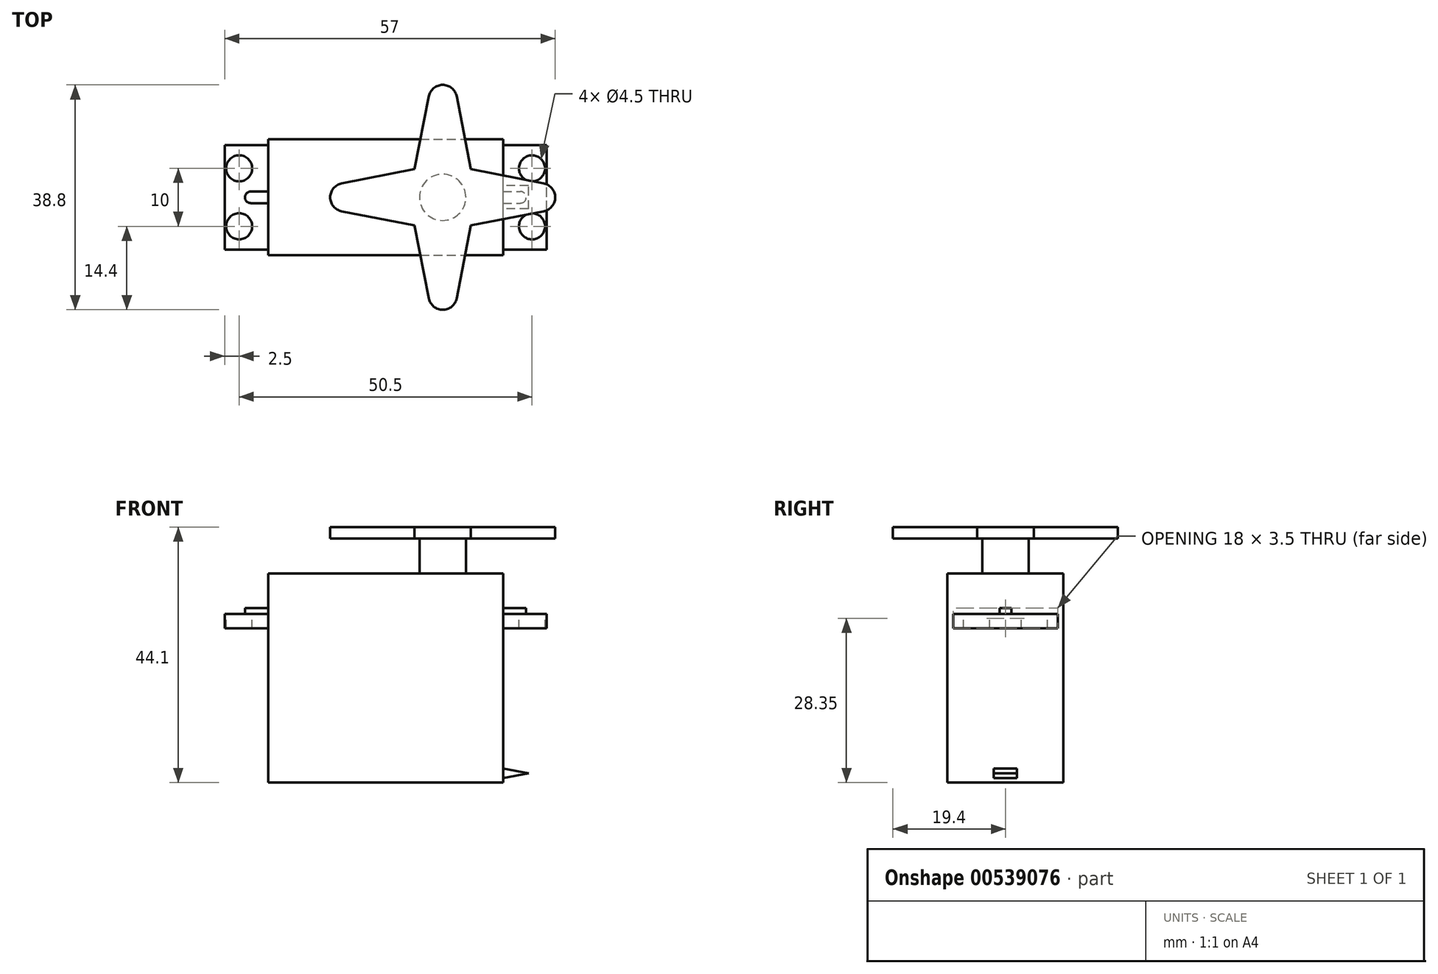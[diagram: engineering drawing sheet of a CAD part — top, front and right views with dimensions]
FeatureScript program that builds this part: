
annotation { "Feature Type Name" : "Feature", "Feature Type Description" : "" }
export const myFeature = defineFeature(function(context is Context, id is Id, definition is map)
    precondition{}
    {
        {
            var Q0;
            Q0=qCreatedBy(makeId("Front.planeOp"),FACE);
            var sketch = newSketch(context, id + "F0", { "sketchPlane" : qUnion([Q0])});
            skLineSegment(sketch, "E0.bottom", {"start": v(0, 0) * mm, "end": v(40.5, 0) * mm});
            skLineSegment(sketch, "E0.top", {"start": v(0, 36.1) * mm, "end": v(40.5, 36.1) * mm});
            skLineSegment(sketch, "E0.left", {"start": v(0, 0) * mm, "end": v(0, 36.1) * mm});
            skLineSegment(sketch, "E0.right", {"start": v(40.5, 0) * mm, "end": v(40.5, 36.1) * mm});
            skLineSegment(sketch, "E1.bottom", {"start": v(40.5, 26.6) * mm, "end": v(48, 26.6) * mm});
            skLineSegment(sketch, "E1.top", {"start": v(40.5, 29.1) * mm, "end": v(48, 29.1) * mm});
            skLineSegment(sketch, "E1.left", {"start": v(40.5, 26.6) * mm, "end": v(40.5, 29.1) * mm});
            skLineSegment(sketch, "E1.right", {"start": v(48, 26.6) * mm, "end": v(48, 29.1) * mm});
            skLineSegment(sketch, "E2.bottom", {"start": v(0, 26.6) * mm, "end": v(-7.5, 26.6) * mm});
            skLineSegment(sketch, "E2.top", {"start": v(0, 29.1) * mm, "end": v(-7.5, 29.1) * mm});
            skLineSegment(sketch, "E2.left", {"start": v(0, 26.6) * mm, "end": v(0, 29.1) * mm});
            skLineSegment(sketch, "E2.right", {"start": v(-7.5, 26.6) * mm, "end": v(-7.5, 29.1) * mm});
            skLineSegment(sketch, "E3", {"start": v(40.5, 2.42) * mm, "end": v(44.9, 1.62) * mm});
            skLineSegment(sketch, "E4", {"start": v(44.9, 1.62) * mm, "end": v(40.5, 0.82) * mm});
            skLineSegment(sketch, "E5", {"start": v(30.1, 44.1) * mm, "end": v(30.1, 36.1) * mm, "construction": true});
            skSolve(sketch);
        }
        {
            var Q0;
            {var subQ3=sQuery(id+"F0.wireOp",EDGE,"E0.bottom");Q0=makeQuery(id+"F0.imprint","IMPRINT",FACE,{"disambiguationData":[TD([[makeQuery(id+"F0.imprint","IMPRINT",EDGE,{"derivedFrom":subQ3}),1.0]])]});}
            extrude(context, id + "F1", {"entities" : qUnion([Q0]), "depth" : 20 * mm, "offsetDistance" : 25 * mm, "symmetric" : true});
        }
        {
            var Q0;
            Q0=makeQuery(id+"F0.imprint","IMPRINT",FACE,{"disambiguationData":[TD([[makeQuery(id+"F0.imprint","IMPRINT",EDGE,{"derivedFrom":sQuery(id+"F0.wireOp",EDGE,"E2.bottom")}),-1.0]])]});
            var Q1;
            Q1=makeQuery(id+"F0.imprint","IMPRINT",FACE,{"disambiguationData":[TD([[makeQuery(id+"F0.imprint","IMPRINT",EDGE,{"derivedFrom":sQuery(id+"F0.wireOp",EDGE,"E1.bottom")}),1.0]])]});
            extrude(context, id + "F2", {"entities" : qUnion([Q0, Q1]), "operationType" : NewBodyOperationType.ADD, "depth" : 18 * mm, "offsetDistance" : 25 * mm, "symmetric" : true});
        }
        {
            var Q0;
            {var subQ0=sQuery(id+"F0.wireOp",EDGE,"E3");Q0=makeQuery(id+"F0.imprint","IMPRINT",FACE,{"disambiguationData":[TD([[makeQuery(id+"F0.imprint","IMPRINT",EDGE,{"derivedFrom":subQ0}),-1.0]])]});}
            extrude(context, id + "F3", {"entities" : qUnion([Q0]), "operationType" : NewBodyOperationType.ADD, "depth" : 4 * mm, "offsetDistance" : 25 * mm, "symmetric" : true});
        }
        {
            var Q0;
            Q0=qCreatedBy(makeId("Top.planeOp"),FACE);
            var Q1;
            Q1=sQuery(id+"F0.wireOp",VERTEX,"E5.start");
            cPlane(context, id + "F4", {"entities" : qUnion([Q0, Q1]), "cplaneType" : CPlaneType.PLANE_POINT, "offset" : 25 * mm, "width" : 150 * mm, "height" : 150 * mm});
        }
        {
            var Q0;
            Q0=qCreatedBy(id+"F4.planeOp",FACE);
            var sketch = newSketch(context, id + "F5", { "sketchPlane" : qUnion([Q0])});
            skCircle(sketch, "E6", {"center": v(30.1, 0) * mm, "radius": 4 * mm});
            skCircle(sketch, "E7", {"center": v(30.1, 0) * mm, "radius": 29.7 * mm, "construction": true});
            skLineSegment(sketch, "E8", {"start": v(30.1, 29.7) * mm, "end": v(25.24, 4.86) * mm});
            skLineSegment(sketch, "E9", {"start": v(25.24, 4.86) * mm, "end": v(0.4, 0) * mm});
            skLineSegment(sketch, "E10", {"start": v(0.4, 0) * mm, "end": v(25.24, -4.86) * mm});
            skLineSegment(sketch, "E11", {"start": v(25.24, -4.86) * mm, "end": v(30.1, -29.7) * mm});
            skLineSegment(sketch, "E12", {"start": v(30.1, -29.7) * mm, "end": v(34.96, -4.86) * mm});
            skLineSegment(sketch, "E13", {"start": v(34.96, -4.86) * mm, "end": v(59.8, 0) * mm});
            skLineSegment(sketch, "E14", {"start": v(59.8, 0) * mm, "end": v(34.96, 4.86) * mm});
            skLineSegment(sketch, "E15", {"start": v(34.96, 4.86) * mm, "end": v(30.1, 29.7) * mm});
            skLineSegment(sketch, "E16", {"start": v(34.96, 4.86) * mm, "end": v(25.24, -4.86) * mm, "construction": true});
            skLineSegment(sketch, "E17", {"start": v(25.24, 4.86) * mm, "end": v(34.96, -4.86) * mm, "construction": true});
            skCircle(sketch, "E18", {"center": v(30.1, 0) * mm, "radius": 19.4 * mm, "construction": true});
            skLineSegment(sketch, "E19.bottom", {"start": v(34.35, 8) * mm, "end": v(25.85, 8) * mm, "construction": true});
            skLineSegment(sketch, "E19.top", {"start": v(34.35, -8) * mm, "end": v(25.85, -8) * mm, "construction": true});
            skLineSegment(sketch, "E19.left", {"start": v(34.35, 8) * mm, "end": v(34.35, -8) * mm, "construction": true});
            skLineSegment(sketch, "E19.right", {"start": v(25.85, 8) * mm, "end": v(25.85, -8) * mm, "construction": true});
            skLineSegment(sketch, "E20.bottom", {"start": v(38.1, 4.25) * mm, "end": v(22.1, 4.25) * mm, "construction": true});
            skLineSegment(sketch, "E20.top", {"start": v(38.1, -4.25) * mm, "end": v(22.1, -4.25) * mm, "construction": true});
            skLineSegment(sketch, "E20.left", {"start": v(38.1, 4.25) * mm, "end": v(38.1, -4.25) * mm, "construction": true});
            skLineSegment(sketch, "E20.right", {"start": v(22.1, 4.25) * mm, "end": v(22.1, -4.25) * mm, "construction": true});
            skCircle(sketch, "E21", {"center": v(13.15, 0) * mm, "radius": 2.45 * mm});
            skCircle(sketch, "E22", {"center": v(30.1, 16.95) * mm, "radius": 2.45 * mm});
            skCircle(sketch, "E23", {"center": v(47.05, 0) * mm, "radius": 2.45 * mm});
            skCircle(sketch, "E24", {"center": v(30.1, -16.95) * mm, "radius": 2.45 * mm});
            skSolve(sketch);
        }
        {
            var Q0;
            Q0=makeQuery(id+"F5.imprint","IMPRINT",FACE,{"disambiguationData":[TD([[makeQuery(id+"F5.imprint","IMPRINT",EDGE,{"derivedFrom":sQuery(id+"F5.wireOp",EDGE,"E6")}),1.0]])]});
            extrude(context, id + "F6", {"entities" : qUnion([Q0]), "operationType" : NewBodyOperationType.ADD, "endBound" : BoundingType.UP_TO_NEXT, "oppositeDirection" : true, "depth" : 25 * mm, "offsetDistance" : 25 * mm});
        }
        {
            var Q0;
            Q0=makeQuery(id+"F5.imprint","IMPRINT",FACE,{"disambiguationData":[TD([[makeQuery(id+"F5.imprint","IMPRINT",EDGE,{"derivedFrom":sQuery(id+"F5.wireOp",EDGE,"E6")}),-1.0]])]});
            var Q1;
            {var subQ0=sQuery(id+"F5.wireOp",EDGE,"E22");var subQ1=makeQuery(id+"F5.imprint","INTERSECT",VERTEX,{"derivedFrom":[sQuery(id+"F5.wireOp",EDGE,"E8"),subQ0]});Q1=makeQuery(id+"F5.imprint","IMPRINT",FACE,{"disambiguationData":[TD([[makeQuery(id+"F5.imprint","IMPRINT",EDGE,{"disambiguationData":[TD([[subQ1,1.0]])],"derivedFrom":subQ0}),1.0]])]});}
            var Q2;
            {var subQ0=sQuery(id+"F5.wireOp",EDGE,"E23");var subQ1=makeQuery(id+"F5.imprint","INTERSECT",VERTEX,{"derivedFrom":[sQuery(id+"F5.wireOp",EDGE,"E13"),subQ0]});Q2=makeQuery(id+"F5.imprint","IMPRINT",FACE,{"disambiguationData":[TD([[makeQuery(id+"F5.imprint","IMPRINT",EDGE,{"disambiguationData":[TD([[subQ1,1.0]])],"derivedFrom":subQ0}),1.0]])]});}
            var Q3;
            {var subQ0=sQuery(id+"F5.wireOp",EDGE,"E24");var subQ1=makeQuery(id+"F5.imprint","INTERSECT",VERTEX,{"derivedFrom":[sQuery(id+"F5.wireOp",EDGE,"E11"),subQ0]});Q3=makeQuery(id+"F5.imprint","IMPRINT",FACE,{"disambiguationData":[TD([[makeQuery(id+"F5.imprint","IMPRINT",EDGE,{"disambiguationData":[TD([[subQ1,-1.0]])],"derivedFrom":subQ0}),1.0]])]});}
            var Q4;
            {var subQ0=sQuery(id+"F5.wireOp",EDGE,"E21");var subQ1=makeQuery(id+"F5.imprint","INTERSECT",VERTEX,{"derivedFrom":[sQuery(id+"F5.wireOp",EDGE,"E9"),subQ0]});Q4=makeQuery(id+"F5.imprint","IMPRINT",FACE,{"disambiguationData":[TD([[makeQuery(id+"F5.imprint","IMPRINT",EDGE,{"disambiguationData":[TD([[subQ1,-1.0]])],"derivedFrom":subQ0}),1.0]])]});}
            var Q5;
            Q5=makeQuery(id+"F5.imprint","IMPRINT",FACE,{"disambiguationData":[TD([[makeQuery(id+"F5.imprint","IMPRINT",EDGE,{"derivedFrom":sQuery(id+"F5.wireOp",EDGE,"E6")}),1.0]])]});
            extrude(context, id + "F7", {"entities" : qUnion([Q0, Q1, Q2, Q3, Q4, Q5]), "operationType" : NewBodyOperationType.ADD, "oppositeDirection" : true, "depth" : 2 * mm, "offsetDistance" : 25 * mm});
        }
        {
            var Q0;
            Q0=makeQuery(id+"F2.opExtrude","SWEPT_FACE",FACE,{"disambiguationData":[OSD([sQuery(id+"F0.wireOp",EDGE,"E1.top")])]});
            var sketch = newSketch(context, id + "F8", { "sketchPlane" : qUnion([Q0])});
            skLineSegment(sketch, "E25.bottom", {"start": v(-5, 5) * mm, "end": v(45.5, 5) * mm, "construction": true});
            skLineSegment(sketch, "E25.top", {"start": v(-5, -5) * mm, "end": v(45.5, -5) * mm, "construction": true});
            skLineSegment(sketch, "E25.left", {"start": v(-5, 5) * mm, "end": v(-5, -5) * mm, "construction": true});
            skLineSegment(sketch, "E25.right", {"start": v(45.5, 5) * mm, "end": v(45.5, -5) * mm, "construction": true});
            skPoint(sketch, "E26.0", {"position": v(20.25, 10) * mm});
            skPoint(sketch, "E27.0", {"position": v(40.5, 0) * mm});
            skLineSegment(sketch, "E28", {"start": v(40.5, 0) * mm, "end": v(20.25, 0) * mm, "construction": true});
            skLineSegment(sketch, "E29", {"start": v(20.25, 10) * mm, "end": v(20.25, 0) * mm, "construction": true});
            skLineSegment(sketch, "E30.bottom", {"start": v(40.5, 1) * mm, "end": v(43.5, 1) * mm});
            skLineSegment(sketch, "E30.top", {"start": v(40.5, -1) * mm, "end": v(43.5, -1) * mm});
            skLineSegment(sketch, "E30.left", {"start": v(40.5, 1) * mm, "end": v(40.5, -1) * mm});
            skLineSegment(sketch, "E30.right", {"start": v(44.5, 0) * mm, "end": v(44.5, 0) * mm});
            skLineSegment(sketch, "E31.bottom", {"start": v(0, 1) * mm, "end": v(-3, 1) * mm});
            skLineSegment(sketch, "E31.top", {"start": v(0, -1) * mm, "end": v(-3, -1) * mm});
            skLineSegment(sketch, "E31.left", {"start": v(0, 1) * mm, "end": v(0, -1) * mm});
            skLineSegment(sketch, "E31.right", {"start": v(-4, 0) * mm, "end": v(-4, 0) * mm});
            skPoint(sketch, "E32.visualSharp", {"position": v(-4, -1) * mm});
            skArc(sketch, "E32.filletArc", {"start": v(-4, 0) * mm, "mid": v(-3.7, -0.7) * mm, "end": v(-3, -1) * mm});
            skPoint(sketch, "E33.visualSharp", {"position": v(-4, 1) * mm});
            skArc(sketch, "E33.filletArc", {"start": v(-3, 1) * mm, "mid": v(-3.7, 0.7) * mm, "end": v(-4, 0) * mm});
            skPoint(sketch, "E34.visualSharp", {"position": v(44.5, 1) * mm});
            skArc(sketch, "E34.filletArc", {"start": v(44.5, 0) * mm, "mid": v(44.2, 0.7) * mm, "end": v(43.5, 1) * mm});
            skPoint(sketch, "E35.visualSharp", {"position": v(44.5, -1) * mm});
            skArc(sketch, "E35.filletArc", {"start": v(43.5, -1) * mm, "mid": v(44.2, -0.7) * mm, "end": v(44.5, 0) * mm});
            skSolve(sketch);
        }
        {
            var Q0;
            Q0=sQuery(id+"F8.wireOp",VERTEX,"E25.bottom.start");
            var Q1;
            Q1=sQuery(id+"F8.wireOp",VERTEX,"E25.left.end");
            var Q2;
            Q2=sQuery(id+"F8.wireOp",VERTEX,"E25.bottom.end");
            var Q3;
            Q3=sQuery(id+"F8.wireOp",VERTEX,"E25.right.end");
            var Q4;
            Q4=makeQuery(id+"F1.opExtrude","SWEPT_BODY",BODY,{"disambiguationData":[OSD([sQuery(id+"F0.wireOp",EDGE,"E0.bottom"),sQuery(id+"F0.wireOp",EDGE,"E0.top"),sQuery(id+"F0.wireOp",EDGE,"E0.left"),sQuery(id+"F0.wireOp",EDGE,"E0.right"),sQuery(id+"F0.wireOp",EDGE,"E1.left"),sQuery(id+"F0.wireOp",EDGE,"E2.left")])]});
            hole(context, id + "F9", {"style" : HoleStyle.SIMPLE, "endStyle" : HoleEndStyle.THROUGH, "holeDiameter" : 4.5 * mm, "isTappedThrough" : true, "tappedDepth" : 12 * mm, "tapClearance" : 3, "locations" : qUnion([Q0, Q1, Q2, Q3]), "scope" : qUnion([Q4])});
        }
        {
            var Q0;
            Q0=makeQuery(id+"F8.imprint","IMPRINT",FACE,{"disambiguationData":[TD([[makeQuery(id+"F8.imprint","IMPRINT",EDGE,{"derivedFrom":sQuery(id+"F8.wireOp",EDGE,"E31.bottom")}),1.0]])]});
            var Q1;
            Q1=makeQuery(id+"F8.imprint","IMPRINT",FACE,{"disambiguationData":[TD([[makeQuery(id+"F8.imprint","IMPRINT",EDGE,{"derivedFrom":sQuery(id+"F8.wireOp",EDGE,"E30.bottom")}),-1.0]])]});
            extrude(context, id + "F10", {"entities" : qUnion([Q0, Q1]), "operationType" : NewBodyOperationType.ADD, "depth" : 1 * mm, "offsetDistance" : 25 * mm});
        }
    });
